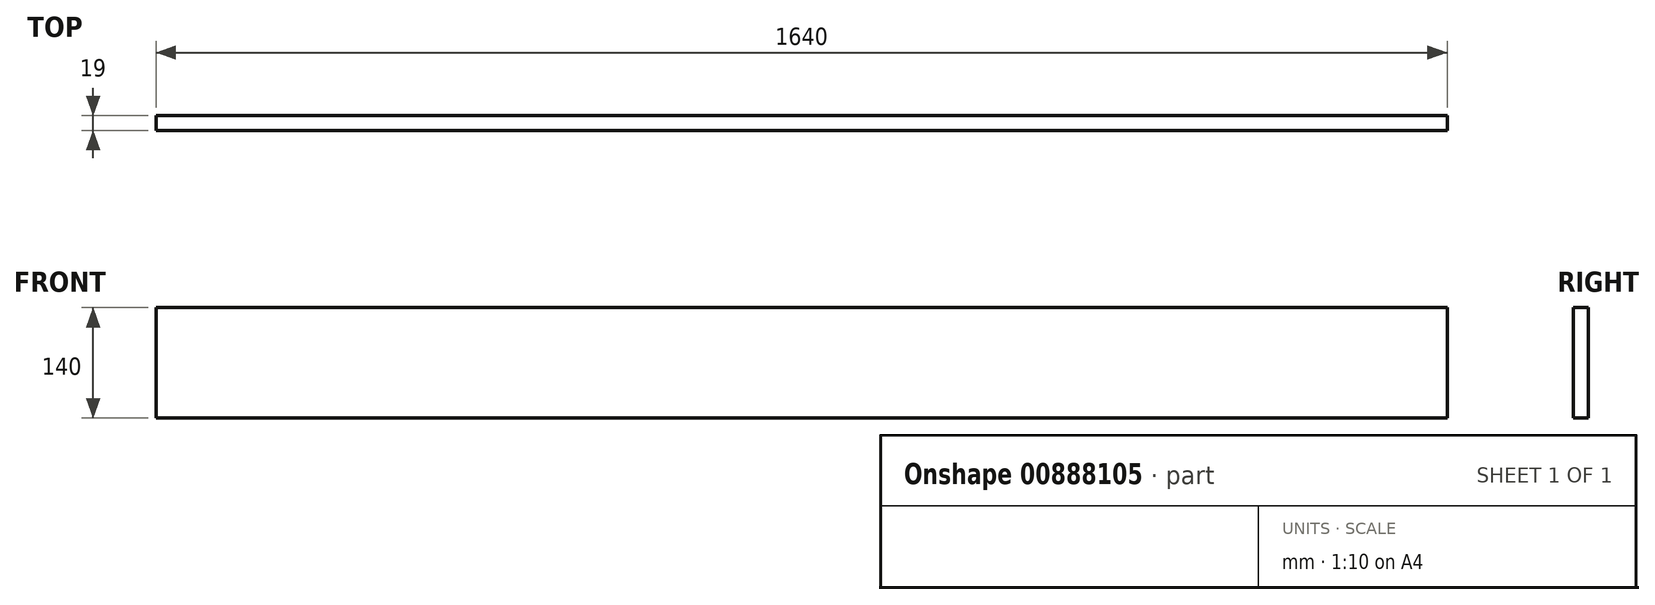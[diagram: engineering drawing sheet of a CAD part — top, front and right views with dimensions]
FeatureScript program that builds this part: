
annotation { "Feature Type Name" : "Feature", "Feature Type Description" : "" }
export const myFeature = defineFeature(function(context is Context, id is Id, definition is map)
    precondition{}
    {
        {
            var Q0;
            Q0=qCreatedBy(makeId("Front.planeOp"),FACE);
            var sketch = newSketch(context, id + "F0", { "sketchPlane" : qUnion([Q0])});
            skLineSegment(sketch, "E0.bottom", {"start": v(-825.5, 32.44) * mm, "end": v(814.5, 32.44) * mm});
            skLineSegment(sketch, "E0.top", {"start": v(-825.5, -107.56) * mm, "end": v(814.5, -107.56) * mm});
            skLineSegment(sketch, "E0.left", {"start": v(-825.5, 32.44) * mm, "end": v(-825.5, -107.56) * mm});
            skLineSegment(sketch, "E0.right", {"start": v(814.5, 32.44) * mm, "end": v(814.5, -107.56) * mm});
            skSolve(sketch);
        }
        {
            var Q0;
            Q0=makeQuery(id+"F0.imprint","IMPRINT",FACE,{"disambiguationData":[TD([[makeQuery(id+"F0.imprint","IMPRINT",EDGE,{"derivedFrom":sQuery(id+"F0.wireOp",EDGE,"E0.bottom")}),-1.0]])]});
            extrude(context, id + "F1", {"entities" : qUnion([Q0]), "depth" : 19 * mm, "offsetDistance" : 25 * mm});
        }
    });
